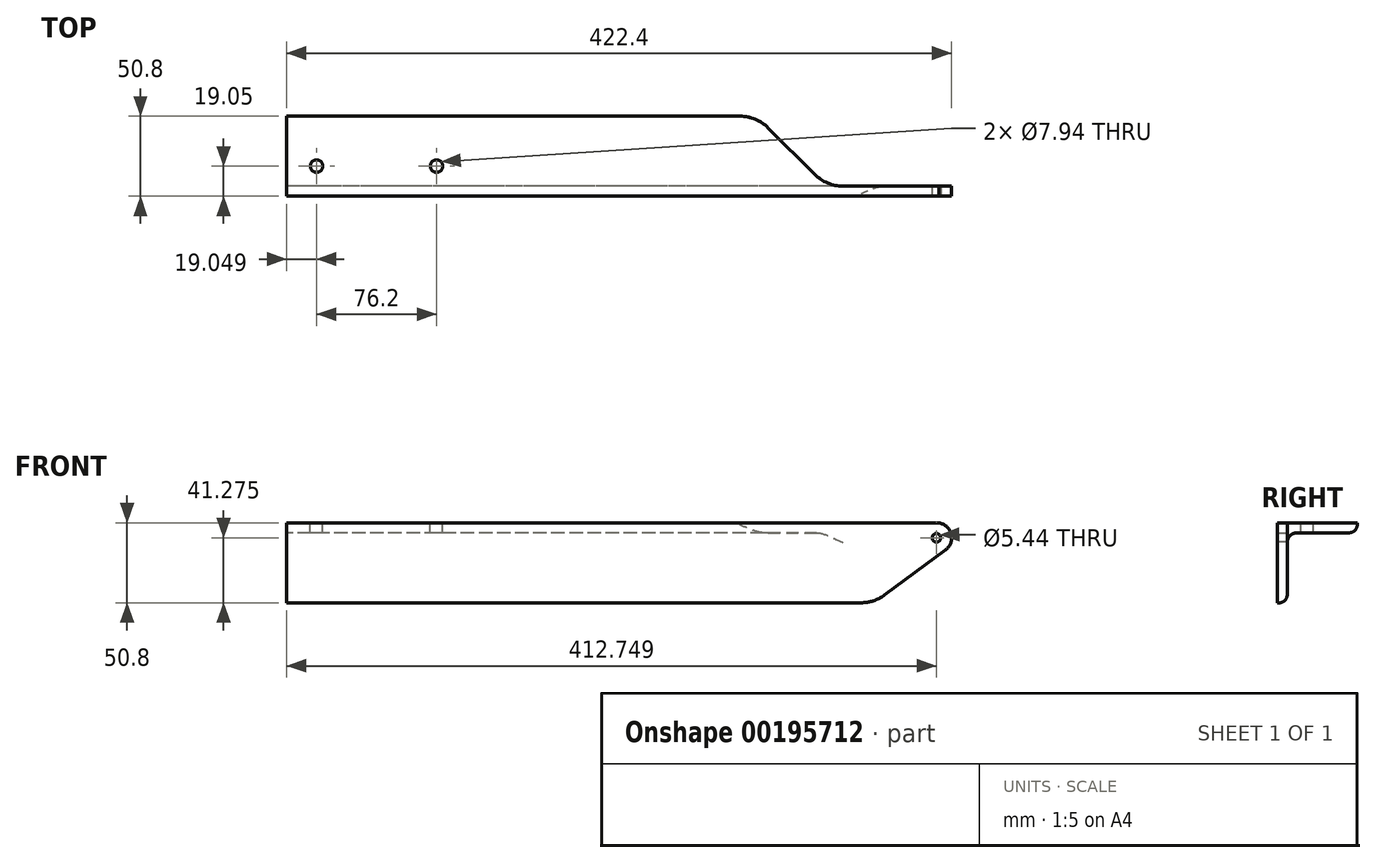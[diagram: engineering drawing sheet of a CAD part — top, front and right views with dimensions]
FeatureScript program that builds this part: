
annotation { "Feature Type Name" : "Feature", "Feature Type Description" : "" }
export const myFeature = defineFeature(function(context is Context, id is Id, definition is map)
    precondition{}
    {
        {
            var Q0;
            Q0=qCreatedBy(makeId("Right.planeOp"),FACE);
            var sketch = newSketch(context, id + "F0", { "sketchPlane" : qUnion([Q0])});
            skLineSegment(sketch, "E0.bottom", {"start": v(0, 0) * mm, "end": v(50.8, 0) * mm});
            skLineSegment(sketch, "E0.top", {"start": v(0, -50.8) * mm, "end": v(1.27, -50.8) * mm});
            skLineSegment(sketch, "E0.left", {"start": v(0, 0) * mm, "end": v(0, -50.8) * mm});
            skLineSegment(sketch, "E0.right", {"start": v(50.8, 0) * mm, "end": v(50.8, -1.27) * mm});
            skLineSegment(sketch, "E1.0", {"start": v(12.7, -6.35) * mm, "end": v(45.72, -6.35) * mm});
            skLineSegment(sketch, "E1.1", {"start": v(6.35, -12.7) * mm, "end": v(6.35, -45.72) * mm});
            skPoint(sketch, "E2.visualSharp", {"position": v(50.8, -6.35) * mm});
            skArc(sketch, "E2.filletArc", {"start": v(45.72, -6.35) * mm, "mid": v(49.31, -4.86) * mm, "end": v(50.8, -1.27) * mm});
            skPoint(sketch, "E3.visualSharp", {"position": v(6.35, -50.8) * mm});
            skArc(sketch, "E3.filletArc", {"start": v(1.27, -50.8) * mm, "mid": v(4.86, -49.31) * mm, "end": v(6.35, -45.72) * mm});
            skPoint(sketch, "E4.visualSharp", {"position": v(6.35, -6.35) * mm});
            skArc(sketch, "E4.filletArc", {"start": v(12.7, -6.35) * mm, "mid": v(8.2, -8.2) * mm, "end": v(6.35, -12.7) * mm});
            skSolve(sketch);
        }
        {
            var Q0;
            Q0=qSketchRegion(id+"F0",true);
            extrude(context, id + "F1", {"entities" : qUnion([Q0]), "endBound" : BoundingType.SYMMETRIC, "depth" : 422.4 * mm});
        }
        {
            var Q0;
            Q0=makeQuery(id+"F1.opExtrude","SWEPT_FACE",FACE,{"disambiguationData":[OSD([sQuery(id+"F0.wireOp",EDGE,"E0.bottom")])]});
            var sketch = newSketch(context, id + "F2", { "sketchPlane" : qUnion([Q0])});
            skLineSegment(sketch, "E5.0", {"start": v(211.2, 19.05) * mm, "end": v(-211.2, 19.05) * mm, "construction": true});
            skLineSegment(sketch, "E6.0", {"start": v(-192.15, 0) * mm, "end": v(-192.15, 50.8) * mm, "construction": true});
            skLineSegment(sketch, "E7.0", {"start": v(-115.95, 0) * mm, "end": v(-115.95, 50.8) * mm, "construction": true});
            skCircle(sketch, "E8", {"center": v(-192.15, 19.05) * mm, "radius": 3.97 * mm});
            skCircle(sketch, "E9", {"center": v(-115.95, 19.05) * mm, "radius": 3.97 * mm});
            skSolve(sketch);
        }
        {
            var Q0;
            Q0=qSketchRegion(id+"F2",true);
            extrude(context, id + "F3", {"entities" : qUnion([Q0]), "operationType" : NewBodyOperationType.REMOVE, "oppositeDirection" : true, "depth" : 25.4 * mm});
        }
        {
            var Q0;
            Q0=makeQuery(id+"F1.opExtrude","SWEPT_FACE",FACE,{"disambiguationData":[OSD([sQuery(id+"F0.wireOp",EDGE,"E0.bottom")])]});
            var sketch = newSketch(context, id + "F4", { "sketchPlane" : qUnion([Q0])});
            skLineSegment(sketch, "E10.0", {"start": v(211.2, 6.35) * mm, "end": v(-211.2, 6.35) * mm, "construction": true});
            skLineSegment(sketch, "E11.0", {"start": v(-211.2, 0) * mm, "end": v(-211.2, 50.8) * mm, "construction": true});
            skLineSegment(sketch, "E12.0", {"start": v(87.25, 0) * mm, "end": v(87.25, 50.8) * mm, "construction": true});
            skLineSegment(sketch, "E13.0", {"start": v(131.7, 0) * mm, "end": v(131.7, 50.8) * mm, "construction": true});
            skLineSegment(sketch, "E14.0", {"start": v(211.2, 0) * mm, "end": v(211.2, 50.8) * mm, "construction": true});
            skLineSegment(sketch, "E15.0", {"start": v(211.2, 50.8) * mm, "end": v(-211.2, 50.8) * mm, "construction": true});
            skLineSegment(sketch, "E16", {"start": v(211.2, 6.35) * mm, "end": v(211.2, 50.8) * mm});
            skLineSegment(sketch, "E17", {"start": v(87.25, 50.8) * mm, "end": v(211.2, 50.8) * mm});
            skLineSegment(sketch, "E18", {"start": v(87.25, 50.8) * mm, "end": v(131.7, 6.35) * mm});
            skLineSegment(sketch, "E19", {"start": v(131.7, 6.35) * mm, "end": v(211.2, 6.35) * mm});
            skSolve(sketch);
        }
        {
            var Q0;
            Q0=qSketchRegion(id+"F4",true);
            extrude(context, id + "F5", {"entities" : qUnion([Q0]), "operationType" : NewBodyOperationType.REMOVE, "endBound" : BoundingType.THROUGH_ALL, "oppositeDirection" : true, "depth" : 25.4 * mm});
        }
        {
            var Q0;
            Q0=makeQuery(id+"F5.boolean.opBoolean","COPY",EDGE,{"derivedFrom":makeQuery(id+"F5.opExtrude","SWEPT_EDGE",EDGE,{"disambiguationData":[OSD([sQuery(id+"F4.wireOp",EDGE,"E18"),sQuery(id+"F4.wireOp",EDGE,"E19")])]})});
            fillet(context, id + "F6", {"entities" : qUnion([Q0]), "radius" : 25.4 * mm, "tangentPropagation" : true, "allowEdgeOverflow" : false});
        }
        {
            var Q0;
            Q0=makeQuery(id+"F1.opExtrude","SWEPT_FACE",FACE,{"disambiguationData":[OSD([sQuery(id+"F0.wireOp",EDGE,"E0.bottom")])]});
            var sketch = newSketch(context, id + "F7", { "sketchPlane" : qUnion([Q0])});
            skLineSegment(sketch, "E20.0", {"start": v(94.69, 43.36) * mm, "end": v(124.26, 13.79) * mm});
            skLineSegment(sketch, "E21.0", {"start": v(76.73, 50.8) * mm, "end": v(-211.2, 50.8) * mm});
            skPoint(sketch, "E22.visualSharp", {"position": v(87.25, 50.8) * mm});
            skArc(sketch, "E22.filletArc", {"start": v(94.69, 43.36) * mm, "mid": v(86.45, 48.87) * mm, "end": v(76.73, 50.8) * mm});
            skLineSegment(sketch, "E23", {"start": v(76.73, 50.8) * mm, "end": v(76.73, 68.3) * mm});
            skLineSegment(sketch, "E24", {"start": v(76.73, 68.3) * mm, "end": v(108.3, 68.3) * mm});
            skLineSegment(sketch, "E25", {"start": v(108.3, 68.3) * mm, "end": v(108.3, 43.36) * mm});
            skLineSegment(sketch, "E26", {"start": v(108.3, 43.36) * mm, "end": v(94.69, 43.36) * mm});
            skSolve(sketch);
        }
        {
            var Q0;
            Q0=qSketchRegion(id+"F7",true);
            extrude(context, id + "F8", {"entities" : qUnion([Q0]), "operationType" : NewBodyOperationType.REMOVE, "endBound" : BoundingType.THROUGH_ALL, "oppositeDirection" : true, "depth" : 25.4 * mm});
        }
        {
            var Q0;
            Q0=makeQuery(id+"F1.opExtrude","SWEPT_FACE",FACE,{"disambiguationData":[OSD([sQuery(id+"F0.wireOp",EDGE,"E0.left")])]});
            var sketch = newSketch(context, id + "F9", { "sketchPlane" : qUnion([Q0])});
            skLineSegment(sketch, "E27.0", {"start": v(-211.2, 0) * mm, "end": v(-211.2, -50.8) * mm, "construction": true});
            skLineSegment(sketch, "E28.0", {"start": v(201.55, 0) * mm, "end": v(201.55, -50.8) * mm, "construction": true});
            skLineSegment(sketch, "E29.0", {"start": v(161.93, 0) * mm, "end": v(161.93, -50.8) * mm, "construction": true});
            skLineSegment(sketch, "E30.0", {"start": v(211.2, -50.8) * mm, "end": v(-211.2, -50.8) * mm});
            skLineSegment(sketch, "E31.0", {"start": v(211.2, 0) * mm, "end": v(-211.2, 0) * mm, "construction": true});
            skLineSegment(sketch, "E32.0", {"start": v(211.2, -9.53) * mm, "end": v(-211.2, -9.53) * mm, "construction": true});
            skCircle(sketch, "E33", {"center": v(201.55, -9.52) * mm, "radius": 2.72 * mm});
            skArc(sketch, "E34", {"start": v(207.28, -17.29) * mm, "mid": v(210.72, -6.5) * mm, "end": v(201.55, 0.13) * mm});
            skLineSegment(sketch, "E35", {"start": v(161.93, -50.8) * mm, "end": v(207.28, -17.29) * mm});
            skLineSegment(sketch, "E36", {"start": v(201.55, 0) * mm, "end": v(201.55, 11.9) * mm});
            skLineSegment(sketch, "E37", {"start": v(161.93, -50.8) * mm, "end": v(161.93, -62.77) * mm});
            skLineSegment(sketch, "E38", {"start": v(201.55, 11.9) * mm, "end": v(237.1, 11.9) * mm});
            skLineSegment(sketch, "E39", {"start": v(161.93, -62.77) * mm, "end": v(237.1, -62.77) * mm});
            skLineSegment(sketch, "E40", {"start": v(237.1, -62.77) * mm, "end": v(237.1, 11.9) * mm});
            skSolve(sketch);
        }
        {
            var Q0;
            Q0=qSketchRegion(id+"F9",true);
            extrude(context, id + "F10", {"entities" : qUnion([Q0]), "operationType" : NewBodyOperationType.REMOVE, "endBound" : BoundingType.THROUGH_ALL, "oppositeDirection" : true, "depth" : 25.4 * mm});
        }
        {
            var Q0;
            Q0=makeQuery(id+"F1.opExtrude","SWEPT_FACE",FACE,{"disambiguationData":[OSD([sQuery(id+"F0.wireOp",EDGE,"E0.left")])]});
            var sketch = newSketch(context, id + "F11", { "sketchPlane" : qUnion([Q0])});
            skLineSegment(sketch, "E41.0", {"start": v(168.65, -45.83) * mm, "end": v(207.28, -17.29) * mm});
            skLineSegment(sketch, "E42.0", {"start": v(153.56, -50.8) * mm, "end": v(-211.2, -50.8) * mm});
            skPoint(sketch, "E43.visualSharp", {"position": v(161.93, -50.8) * mm});
            skArc(sketch, "E43.filletArc", {"start": v(153.56, -50.8) * mm, "mid": v(161.5, -49.53) * mm, "end": v(168.65, -45.83) * mm});
            skLineSegment(sketch, "E44", {"start": v(153.56, -50.8) * mm, "end": v(153.56, -83.13) * mm});
            skLineSegment(sketch, "E45", {"start": v(207.28, -17.29) * mm, "end": v(207.28, -83.13) * mm});
            skLineSegment(sketch, "E46", {"start": v(207.28, -83.13) * mm, "end": v(153.56, -83.13) * mm});
            skSolve(sketch);
        }
        {
            var Q0;
            Q0=qSketchRegion(id+"F11",true);
            extrude(context, id + "F12", {"entities" : qUnion([Q0]), "operationType" : NewBodyOperationType.REMOVE, "endBound" : BoundingType.THROUGH_ALL, "oppositeDirection" : true, "depth" : 25.4 * mm});
        }
    });
